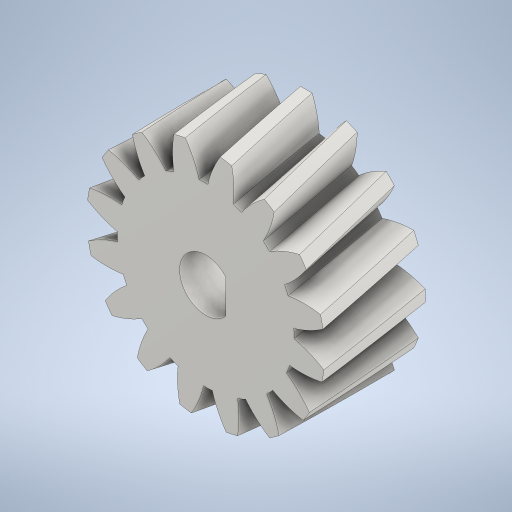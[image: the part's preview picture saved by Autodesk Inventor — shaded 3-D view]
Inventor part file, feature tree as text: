
AUTODESK INVENTOR PART (.ipt)
format: ipt  version: 2023.2 (Build 272271030, 271C)  size: 508,928 bytes
history: native  units: mm (DEFAULTED — no unit token found)
features: plane x3, other x3, sketch x3, extrude x2
ambient origin geometry x8: Origin, YZ Plane, XZ Plane, XY Plane, X Axis, Y Axis, Z Axis, Center Point
bodies: Solid1 (feature_tree)
feature tree (11):
  extrude  "Extrusion1"  Depth=10.0mm TaperAngle=0.0deg
  plane  "Work Plane1"
  plane  "Work Plane2"
  plane  "Work Plane3"
  other  "Spur Gear"
  extrude  "Extrusion2"  Depth=76.2mm TaperAngle=0.0deg
  sketch  "Sketch1"  dims[d0=23.681469mm d1=10.0mm d2=0.0mm]
  sketch  "Sketch2"  dims[d3=20.633469mm d4=76.2mm d5=0.0mm]
  other  "Srf1"
  sketch  "Sketch3"  dims[d6=0.0mm d7=1.963495mm d9=0.0mm d14=0.0mm d15=42.556529mm d16=0.0mm d17=0.0mm d18=0.0mm d19=42.556529mm d20=5.2mm d21=25.4mm d22=0.0mm d24=2.0mm]
  other  "Pitch Diameter"
